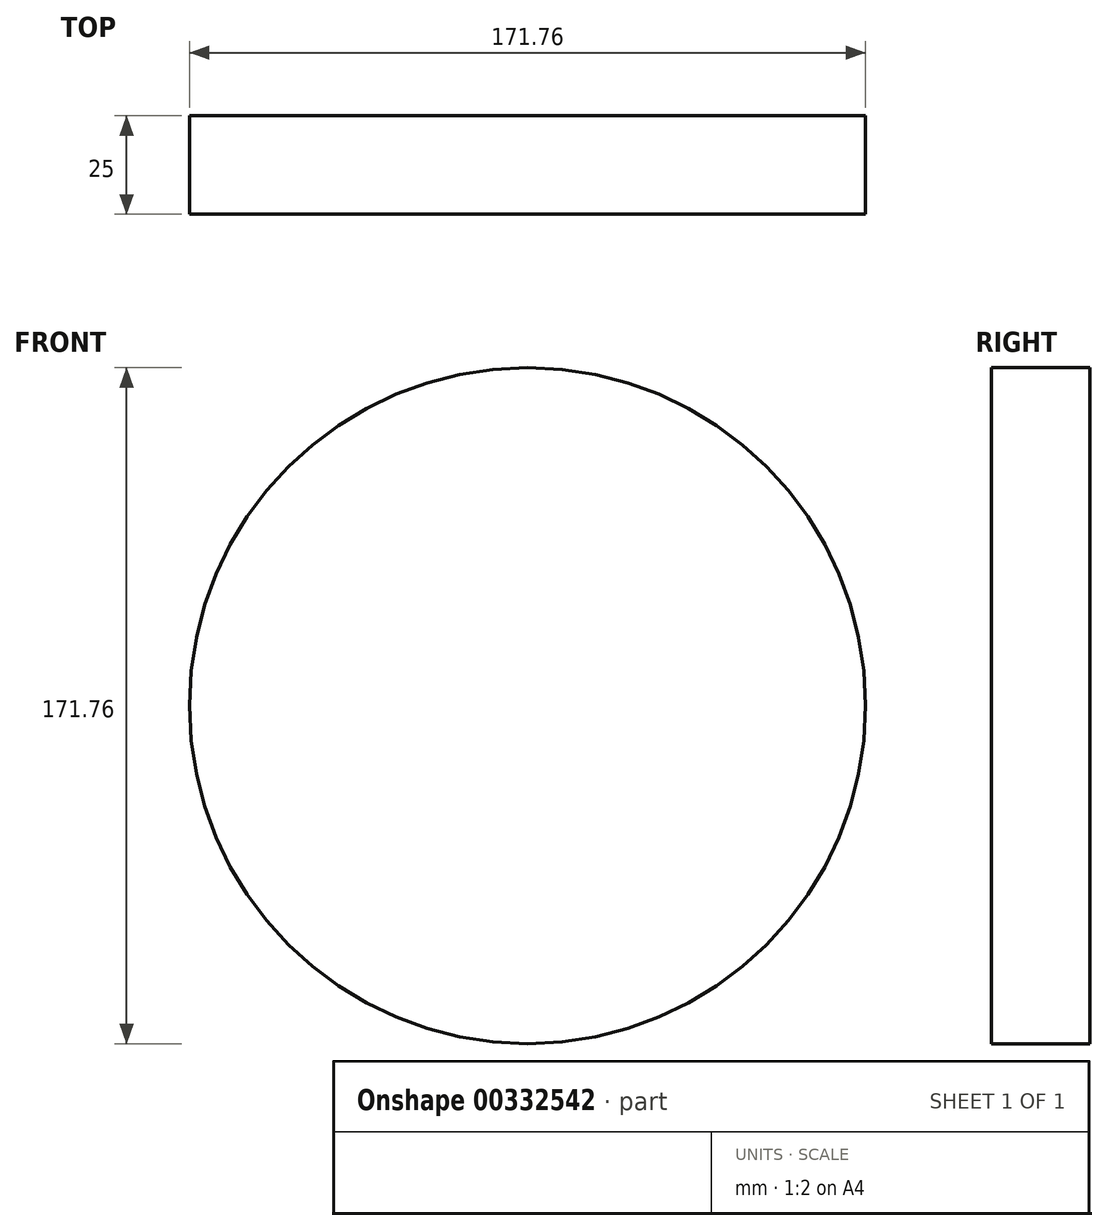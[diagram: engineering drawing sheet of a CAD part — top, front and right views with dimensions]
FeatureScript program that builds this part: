
annotation { "Feature Type Name" : "Feature", "Feature Type Description" : "" }
export const myFeature = defineFeature(function(context is Context, id is Id, definition is map)
    precondition{}
    {
        {
            var Q0;
            Q0=qCreatedBy(makeId("Front.planeOp"),FACE);
            var sketch = newSketch(context, id + "F0", { "sketchPlane" : qUnion([Q0])});
            skCircle(sketch, "E0", {"center": v(0, 0) * mm, "radius": 85.88 * mm});
            skSolve(sketch);
        }
        {
            var Q0;
            Q0=makeQuery(id+"F0.imprint","IMPRINT",FACE,{"disambiguationData":[TD([[makeQuery(id+"F0.imprint","IMPRINT",EDGE,{"derivedFrom":sQuery(id+"F0.wireOp",EDGE,"E0")}),1.0]])]});
            var Q1;
            Q1=sQuery(id+"F0.wireOp",EDGE,"E0");
            extrude(context, id + "F1", {"entities" : qUnion([Q0]), "surfaceEntities" : qUnion([Q1]), "depth" : 25 * mm});
        }
    });
